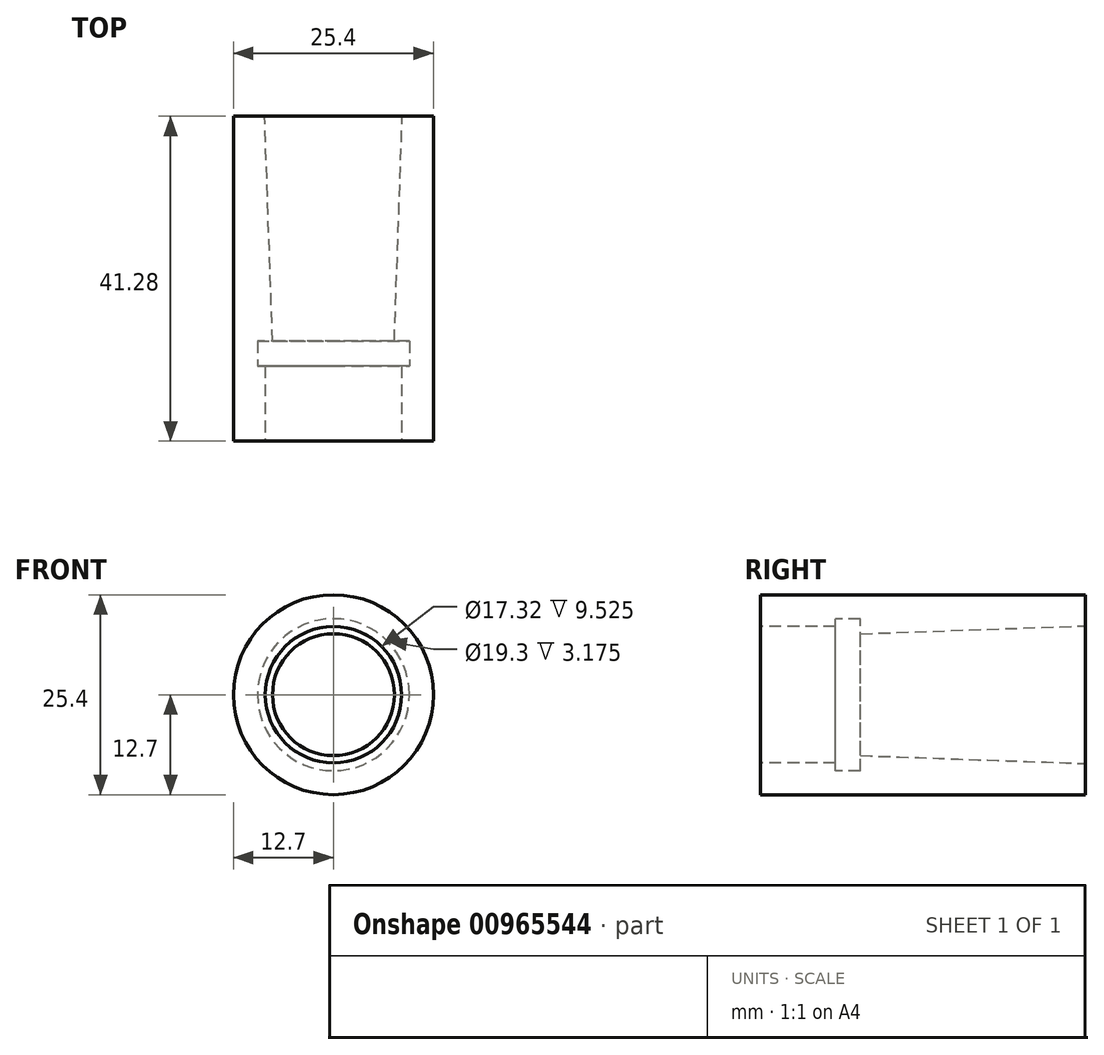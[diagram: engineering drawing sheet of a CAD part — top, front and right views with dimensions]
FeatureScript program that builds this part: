
annotation { "Feature Type Name" : "Feature", "Feature Type Description" : "" }
export const myFeature = defineFeature(function(context is Context, id is Id, definition is map)
    precondition{}
    {
        {
            var Q0;
            Q0=qCreatedBy(makeId("Right.planeOp"),FACE);
            var sketch = newSketch(context, id + "F0", { "sketchPlane" : qUnion([Q0])});
            skLineSegment(sketch, "E0", {"start": v(-89.02, 0) * mm, "end": v(87.7, 0) * mm, "construction": true});
            skLineSegment(sketch, "E1", {"start": v(0, 12.7) * mm, "end": v(41.28, 12.7) * mm});
            skLineSegment(sketch, "E2", {"start": v(41.28, 12.7) * mm, "end": v(41.28, 8.74) * mm});
            skLineSegment(sketch, "E3", {"start": v(0, 8.66) * mm, "end": v(9.53, 8.66) * mm});
            skLineSegment(sketch, "E4", {"start": v(0, 12.7) * mm, "end": v(0, 8.66) * mm});
            skLineSegment(sketch, "E5", {"start": v(9.53, 8.66) * mm, "end": v(9.53, 9.65) * mm});
            skLineSegment(sketch, "E6", {"start": v(9.53, 9.65) * mm, "end": v(12.7, 9.65) * mm});
            skLineSegment(sketch, "E7", {"start": v(12.7, 9.65) * mm, "end": v(12.7, 7.74) * mm});
            skLineSegment(sketch, "E8", {"start": v(12.7, 7.74) * mm, "end": v(41.28, 8.74) * mm});
            skSolve(sketch);
        }
        {
            var Q0;
            Q0 = qSketchRegion(id + "F0", true);
            var Q1;
            Q1=sQuery(id+"F0.wireOp",EDGE,"E0");
            revolve(context, id + "F1", {"surfaceOperationType" : NewSurfaceOperationType.NEW, "entities" : qUnion([Q0]), "axis" : qUnion([Q1]), "revolveType" : RevolveType.FULL});
        }
    });
